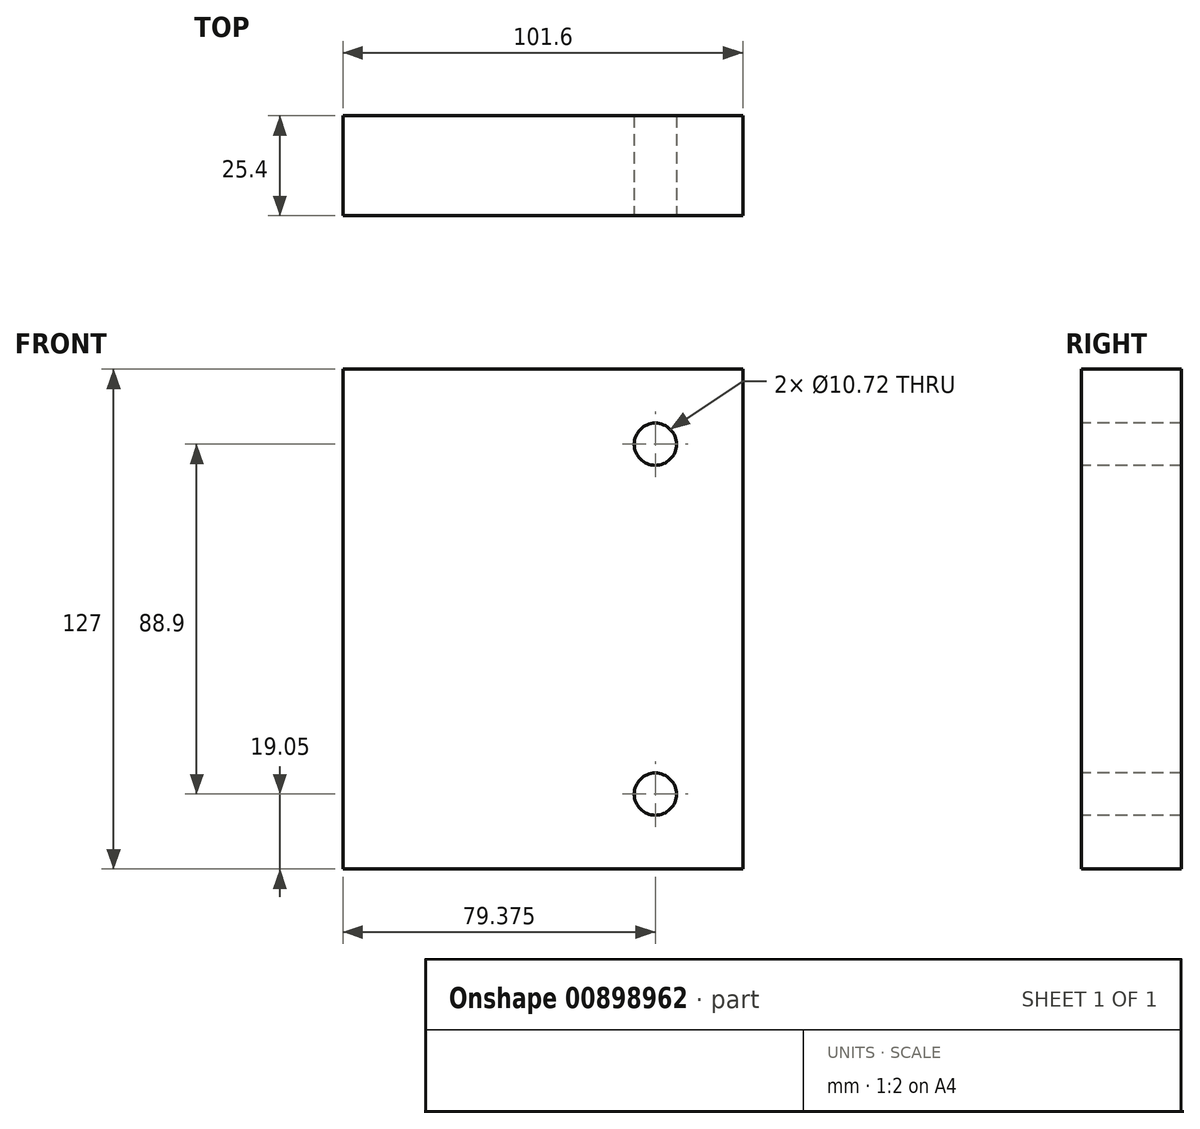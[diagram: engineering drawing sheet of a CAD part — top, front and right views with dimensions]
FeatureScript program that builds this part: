
annotation { "Feature Type Name" : "Feature", "Feature Type Description" : "" }
export const myFeature = defineFeature(function(context is Context, id is Id, definition is map)
    precondition{}
    {
        {
            var Q0;
            Q0=qCreatedBy(makeId("Front.planeOp"),FACE);
            var sketch = newSketch(context, id + "F0", { "sketchPlane" : qUnion([Q0])});
            skLineSegment(sketch, "E0.bottom", {"start": v(-50.8, 63.5) * mm, "end": v(50.8, 63.5) * mm});
            skLineSegment(sketch, "E0.top", {"start": v(-50.8, -63.5) * mm, "end": v(50.8, -63.5) * mm});
            skLineSegment(sketch, "E0.left", {"start": v(-50.8, 63.5) * mm, "end": v(-50.8, -63.5) * mm});
            skLineSegment(sketch, "E0.right", {"start": v(50.8, 63.5) * mm, "end": v(50.8, -63.5) * mm});
            skPoint(sketch, "E0.middle", {"position": v(0, 0) * mm});
            skSolve(sketch);
        }
        {
            var Q0;
            Q0 = qSketchRegion(id + "F0", true);
            extrude(context, id + "F1", {"entities" : qUnion([Q0]), "endBound" : BoundingType.SYMMETRIC, "depth" : 25.4 * mm, "offsetDistance" : 25.4 * mm});
        }
        {
            var Q0;
            Q0=makeQuery(id+"F1.opExtrude","CAP_FACE",FACE,{"disambiguationData":[OSD([sQuery(id+"F0.wireOp",EDGE,"E0.bottom"),sQuery(id+"F0.wireOp",EDGE,"E0.top"),sQuery(id+"F0.wireOp",EDGE,"E0.left"),sQuery(id+"F0.wireOp",EDGE,"E0.right")])],"isStart":false});
            var sketch = newSketch(context, id + "F2", { "sketchPlane" : qUnion([Q0])});
            skLineSegment(sketch, "E1.0", {"start": v(28.58, 63.5) * mm, "end": v(28.57, -63.5) * mm, "construction": true});
            skLineSegment(sketch, "E2", {"start": v(-98.73, 0) * mm, "end": v(107.28, 0) * mm, "construction": true});
            skLineSegment(sketch, "E3.0", {"start": v(-98.73, -44.45) * mm, "end": v(107.28, -44.45) * mm, "construction": true});
            skPoint(sketch, "E4", {"position": v(28.57, -44.45) * mm});
            skPoint(sketch, "E5.MirrorP", {"position": v(28.58, 44.45) * mm});
            skSolve(sketch);
        }
        {
            var Q0;
            Q0=sQuery(id+"F2.wireOp",VERTEX,"E5.MirrorP");
            var Q1;
            Q1=sQuery(id+"F2.wireOp",VERTEX,"E4");
            var Q2;
            Q2=makeQuery(id+"F1.opExtrude","SWEPT_BODY",BODY,{"disambiguationData":[OSD([sQuery(id+"F0.wireOp",EDGE,"E0.bottom"),sQuery(id+"F0.wireOp",EDGE,"E0.top"),sQuery(id+"F0.wireOp",EDGE,"E0.left"),sQuery(id+"F0.wireOp",EDGE,"E0.right")])]});
            hole(context, id + "F3", {"style" : HoleStyle.SIMPLE, "endStyle" : HoleEndStyle.THROUGH, "standardTappedOrClearance" : lookupTablePath({ "standard" : "ANSI", "engagement" : "75%", "pitch" : "13 tpi", "size" : "1/2", "type" : "Tapped" }), "standardBlindInLast" : lookupTablePath({ "standard" : "ANSI", "engagement" : "75%", "pitch" : "13 tpi", "size" : "1/2", "type" : "Tapped" }), "holeDiameter" : 10.72 * mm, "majorDiameter" : 12.7 * mm, "showTappedDepth" : true, "isTappedThrough" : true, "tappedDepth" : 7.9 * mm, "tapClearance" : 3, "startFromSketch" : true, "locations" : qUnion([Q0, Q1]), "scope" : qUnion([Q2])});
        }
    });
